# Revit family: Faucet-Wall_Mount-Lavatory-KOHLER-Composed-K-73061IN_1
name_source: partatom
category: Plumbing Fixtures
units: mm (PartAtom-declared; Revit-internal decimal feet)

## family parameters
Cut with Voids When Loaded = No
Host = Face
OmniClass Number = 23.31.11.00
OmniClass Title = Faucets
Part Type = Normal
Room Calculation Point = No
Round Connector Dimension = Use Diameter
Shared = No

## types (2) — shared parameters
ADA Compliant = No
Assembly Code = D2010
CW Connection = Yes
Cold Water Inlet = Cold Water Inlet
Date Modified = 02/15/2023
Default Elevation = 36"
Description = Single Handle Wall-Mount Lavatory Faucet
Flow Rate = 2 GPM
HW Connection = Yes
Height = 3 5/16"
Hot Water Inlet = Hot Water Inlet
Length = 6 5/8"
Manufacturer = Kohler Co.
Master Format 2014 = 22 41 39
Master Format 2014 Name = Residential Faucets, Supplies, and Trim
Material = Premium Metal Construction
Pressure = 45.00 psi
Product Name = Composed
Spout Reach = 6 5/8"
URL = https://www.kohler.co.in
Vent Connection = No
Waste Connection = No
Waste Water Outlet = Waste Water Outlet
WaterSense Certified = No
Width = 9 1/16"

## per-type parameters (varying)
| type | Drain Included | Finish | Model | Type |
| Without Drain, CP-Polished Chrome | No | Kohler-Metal-CP-Polished_Chrome | K-73061IN-4ND-CP | 2 |
| With Drain, BL-Matte Black | Yes | Kohler-Metal-BL-Matte_Black | K-73061IN-7-BL | 1 |

## geometry (parser evidence)
native form markers: Sweep x5
no freeform markers — native parametric forms only
